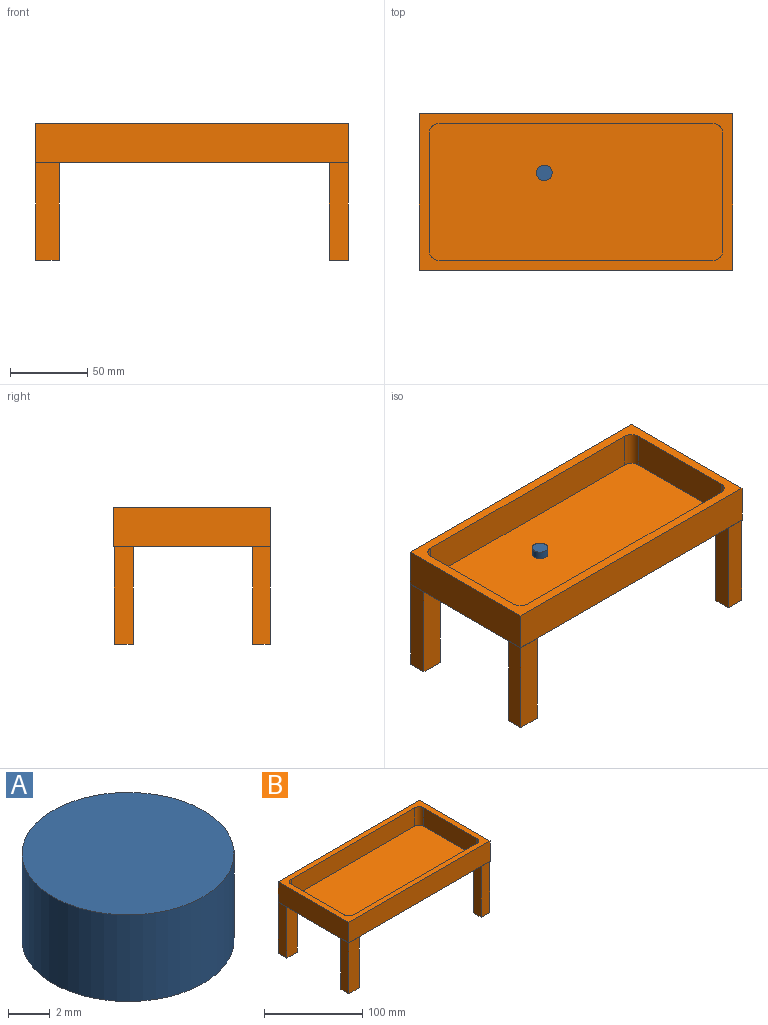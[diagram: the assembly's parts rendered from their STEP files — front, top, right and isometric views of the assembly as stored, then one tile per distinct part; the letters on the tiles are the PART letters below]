
ASSEMBLY  parts=2 mates=1
PART A: 3 faces, bbox 10.2x10.2x5.1 mm
  f0: cylinder r=5.08mm len=10.16mm, axis (0,0,-1), area 162.1mm2, adj f1,f2
  f1: plane 10.16x10.16mm, normal (0,0,1), area 81.1mm2, adj f0
  f2: plane 10.16x10.16mm, normal (0,0,-1), area 81.1mm2, adj f0
PART B: 35 faces, bbox 203.2x101.6x88.9 mm
  f0: plane 203.2x101.6mm, normal (0,0,-1), area 19999.7mm2, adj f3,f4,f5,f12,f15,f16,f17,f18
  f1: plane 76.2x22.86mm, normal (-1,0,0), area 1741.9mm2, adj f7,f8,f13,f14
  f2: plane 76.2x22.86mm, normal (1,0,0), area 1741.9mm2, adj f10,f11,f13,f14
  f3: plane 101.6x25.4mm, normal (-1,0,0), area 2580.6mm2, adj f0,f4,f12,f13
  f4: plane 203.2x25.4mm, normal (0,-1,0), area 5161.3mm2, adj f0,f3,f5,f13
  f5: plane 101.6x25.4mm, normal (1,0,0), area 2580.6mm2, adj f0,f4,f12,f13
  f6: plane 177.8x22.86mm, normal (0,-1,0), area 4064.5mm2, adj f7,f11,f13,f14
  f7: cylinder r=6.35mm len=22.86mm, axis (0,0,-1), area 228mm2, adj f1,f6,f13,f14
  f8: cylinder r=6.35mm len=22.86mm, axis (0,0,-1), area 228mm2, adj f1,f9,f13,f14
  f9: plane 177.8x22.86mm, normal (0,1,0), area 4064.5mm2, adj f8,f10,f13,f14
  f10: cylinder r=6.35mm len=22.86mm, axis (0,0,-1), area 228mm2, adj f2,f9,f13,f14
  f11: cylinder r=6.35mm len=22.86mm, axis (0,0,-1), area 228mm2, adj f2,f6,f13,f14
  f12: plane 203.2x25.4mm, normal (0,1,0), area 5161.3mm2, adj f0,f3,f5,f13
  f13: plane 203.2x101.6mm, normal (0,0,1), area 3744.3mm2, adj f1,f2,f3,f4,f5,f6,f7,f8
  f14: plane 190.5x88.9mm, normal (0,0,1), area 16900.8mm2, adj f1,f2,f6,f7,f8,f9,f10,f11
  f15: plane 63.5x15.12mm, normal (0,-1,0), area 959.9mm2, adj f0,f16,f18,f19
  f16: plane 63.5x11.25mm, normal (1,0,0), area 714.1mm2, adj f0,f15,f17,f19
  f17: plane 63.5x15.12mm, normal (0,1,0), area 959.9mm2, adj f0,f16,f18,f19
  f18: plane 63.5x11.25mm, normal (-1,0,0), area 714.1mm2, adj f0,f15,f17,f19
  f19: plane 15.12x11.25mm, normal (0,0,-1), area 170mm2, adj f15,f16,f17,f18
  f20: plane 63.5x12.17mm, normal (1,0,0), area 772.6mm2, adj f0,f21,f23,f24
  f21: plane 63.5x15.12mm, normal (0,1,0), area 959.9mm2, adj f0,f20,f22,f24
  f22: plane 63.5x12.17mm, normal (-1,0,0), area 772.6mm2, adj f0,f21,f23,f24
  f23: plane 63.5x15.12mm, normal (0,-1,0), area 959.9mm2, adj f0,f20,f22,f24
  f24: plane 15.12x12.17mm, normal (0,0,-1), area 183.9mm2, adj f20,f21,f22,f23
  f25: plane 63.5x12.54mm, normal (0,1,0), area 796mm2, adj f0,f26,f28,f29
  f26: plane 63.5x12.17mm, normal (-1,0,0), area 772.6mm2, adj f0,f25,f27,f29
  f27: plane 63.5x12.54mm, normal (0,-1,0), area 796mm2, adj f0,f26,f28,f29
  f28: plane 63.5x12.17mm, normal (1,0,0), area 772.6mm2, adj f0,f25,f27,f29
  f29: plane 12.54x12.17mm, normal (0,0,-1), area 152.5mm2, adj f25,f26,f27,f28
  f30: plane 63.5x11.25mm, normal (1,0,0), area 714.1mm2, adj f0,f31,f33,f34
  f31: plane 63.5x12.35mm, normal (0,1,0), area 784.3mm2, adj f0,f30,f32,f34
  f32: plane 63.5x11.25mm, normal (-1,0,0), area 714.1mm2, adj f0,f31,f33,f34
  f33: plane 63.5x12.35mm, normal (0,-1,0), area 784.3mm2, adj f0,f30,f32,f34
  f34: plane 12.35x11.25mm, normal (0,0,-1), area 138.9mm2, adj f30,f31,f32,f33
PLACE A t=(34.08,-58.49,19.15)mm
PLACE B t=(-8.85,-4.23,16.61)mm
MATE planar A.f0 <-> B.f14  axis (0,0,-1) through (-29.43,8.21,19.15)mm
